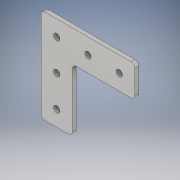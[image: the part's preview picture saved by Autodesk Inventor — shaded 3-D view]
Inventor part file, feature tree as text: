
AUTODESK INVENTOR PART (.ipt)
format: ipt  version: 2018 (Build 220112000, 112)  size: 137,216 bytes
history: native  units: in
note: dims shown in document units (in); Inventor stores cm internally (conversion verified against a paired STEP export)
features: extrude x2, sketch x2, fillet x1
ambient origin geometry x8: Origin, YZ Plane, XZ Plane, XY Plane, X Axis, Y Axis, Z Axis, Center Point
bodies: Solid1 (feature_tree)
feature tree (5):
  extrude  "Extrusion1"  Depth=3.0in
  extrude  "Extrusion2"  Depth=1.0in
  fillet  "Fillet1"  Radius=0.125in
  sketch  "Sketch1"  dims[d0=1.0in d1=3.0in]
  sketch  "Sketch2"  dims[d2=3.0in d3=1.0in d4=0.125in d5=0.0in d6=0.5in d7=1.0in d8=1.0in d11=1.0in d12=1.0in d13=0.2031in d14=0.125in d15=0.0in d16=0.125in]
